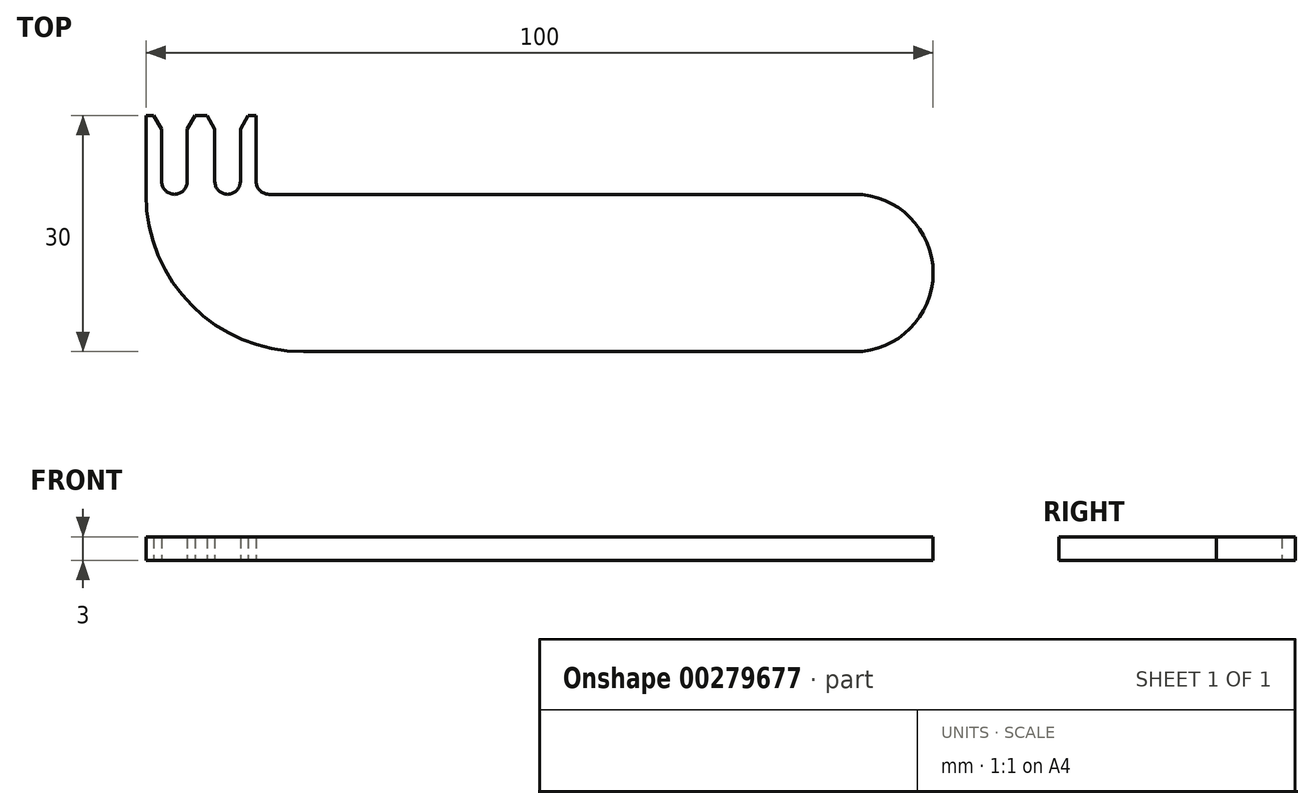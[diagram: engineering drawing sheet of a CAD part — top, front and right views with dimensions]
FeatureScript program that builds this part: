
annotation { "Feature Type Name" : "Feature", "Feature Type Description" : "" }
export const myFeature = defineFeature(function(context is Context, id is Id, definition is map)
    precondition{}
    {
        {
            var Q0;
            Q0=qCreatedBy(makeId("Top.planeOp"),FACE);
            var sketch = newSketch(context, id + "F0", { "sketchPlane" : qUnion([Q0])});
            skLineSegment(sketch, "E0.bottom", {"start": v(0, 0) * mm, "end": v(48.75, 0) * mm});
            skLineSegment(sketch, "E0.top", {"start": v(-25.62, 20) * mm, "end": v(48.75, 20) * mm});
            skLineSegment(sketch, "E1", {"start": v(-41.25, 30) * mm, "end": v(-41.25, 20) * mm});
            skLineSegment(sketch, "E2", {"start": v(-21.25, 0) * mm, "end": v(0, 0) * mm});
            skLineSegment(sketch, "E3.0", {"start": v(-39.25, 28.27) * mm, "end": v(-39.25, 21.62) * mm});
            skLineSegment(sketch, "E4", {"start": v(-41.25, 30) * mm, "end": v(-40.25, 30) * mm});
            skPoint(sketch, "E5.orphan", {"position": v(-39.25, 20) * mm});
            skLineSegment(sketch, "E6", {"start": v(-37.62, 20) * mm, "end": v(-37.62, 20) * mm});
            skLineSegment(sketch, "E7", {"start": v(-36, 21.62) * mm, "end": v(-36, 28.27) * mm});
            skLineSegment(sketch, "E8", {"start": v(-35, 30) * mm, "end": v(-33.5, 30) * mm});
            skLineSegment(sketch, "E9", {"start": v(-32.5, 28.27) * mm, "end": v(-32.5, 21.63) * mm});
            skLineSegment(sketch, "E10", {"start": v(-30.87, 20) * mm, "end": v(-30.87, 20) * mm});
            skLineSegment(sketch, "E11", {"start": v(-29.25, 21.62) * mm, "end": v(-29.25, 28.27) * mm});
            skPoint(sketch, "E11.endSnap0", {"position": v(-40.25, 30) * mm});
            skLineSegment(sketch, "E12", {"start": v(-28.25, 30) * mm, "end": v(-27.25, 30) * mm});
            skLineSegment(sketch, "E13", {"start": v(-27.25, 30) * mm, "end": v(-27.25, 21.63) * mm});
            skPoint(sketch, "E14.orphan", {"position": v(14.2, 20) * mm});
            skPoint(sketch, "E15.visualSharp", {"position": v(-41.25, 0) * mm});
            skArc(sketch, "E15.filletArc", {"start": v(-41.25, 20) * mm, "mid": v(-35.39, 5.86) * mm, "end": v(-21.25, 0) * mm});
            skPoint(sketch, "E16.visualSharp", {"position": v(58.75, 20) * mm});
            skPoint(sketch, "E17.visualSharp", {"position": v(58.75, 0) * mm});
            skPoint(sketch, "E18.visualSharp", {"position": v(-29.25, 20) * mm});
            skArc(sketch, "E18.filletArc", {"start": v(-30.87, 20) * mm, "mid": v(-29.72, 20.48) * mm, "end": v(-29.25, 21.62) * mm});
            skPoint(sketch, "E19.visualSharp", {"position": v(-32.5, 20) * mm});
            skArc(sketch, "E19.filletArc", {"start": v(-32.5, 21.63) * mm, "mid": v(-32.02, 20.48) * mm, "end": v(-30.87, 20) * mm});
            skPoint(sketch, "E20.visualSharp", {"position": v(-36, 20) * mm});
            skArc(sketch, "E20.filletArc", {"start": v(-37.62, 20) * mm, "mid": v(-36.47, 20.48) * mm, "end": v(-36, 21.62) * mm});
            skArc(sketch, "E21.filletArc", {"start": v(-39.25, 21.62) * mm, "mid": v(-38.77, 20.48) * mm, "end": v(-37.62, 20) * mm});
            skPoint(sketch, "E22.visualSharp", {"position": v(-27.25, 20) * mm});
            skArc(sketch, "E22.filletArc", {"start": v(-27.25, 21.63) * mm, "mid": v(-26.77, 20.48) * mm, "end": v(-25.62, 20) * mm});
            skLineSegment(sketch, "E23", {"start": v(-39.25, 28.27) * mm, "end": v(-40.25, 30) * mm});
            skPoint(sketch, "E24.orphan", {"position": v(-39.25, 30) * mm});
            skLineSegment(sketch, "E25", {"start": v(-36, 28.27) * mm, "end": v(-35, 30) * mm});
            skLineSegment(sketch, "E26", {"start": v(-33.5, 30) * mm, "end": v(-32.5, 28.27) * mm});
            skPoint(sketch, "E27.orphan", {"position": v(-36, 30) * mm});
            skPoint(sketch, "E28.orphan", {"position": v(-32.5, 30) * mm});
            skLineSegment(sketch, "E29", {"start": v(-29.25, 28.27) * mm, "end": v(-28.25, 30) * mm});
            skPoint(sketch, "E30.orphan", {"position": v(-29.25, 30) * mm});
            skArc(sketch, "E31", {"start": v(48.75, 0) * mm, "mid": v(58.75, 10) * mm, "end": v(48.75, 20) * mm});
            skSolve(sketch);
        }
        {
            var Q0;
            Q0=makeQuery(id+"F0.imprint","IMPRINT",FACE,{"disambiguationData":[TD([[makeQuery(id+"F0.imprint","IMPRINT",EDGE,{"derivedFrom":sQuery(id+"F0.wireOp",EDGE,"E0.bottom")}),1.0]])]});
            extrude(context, id + "F1", {"entities" : qUnion([Q0]), "depth" : 3 * mm});
        }
    });
